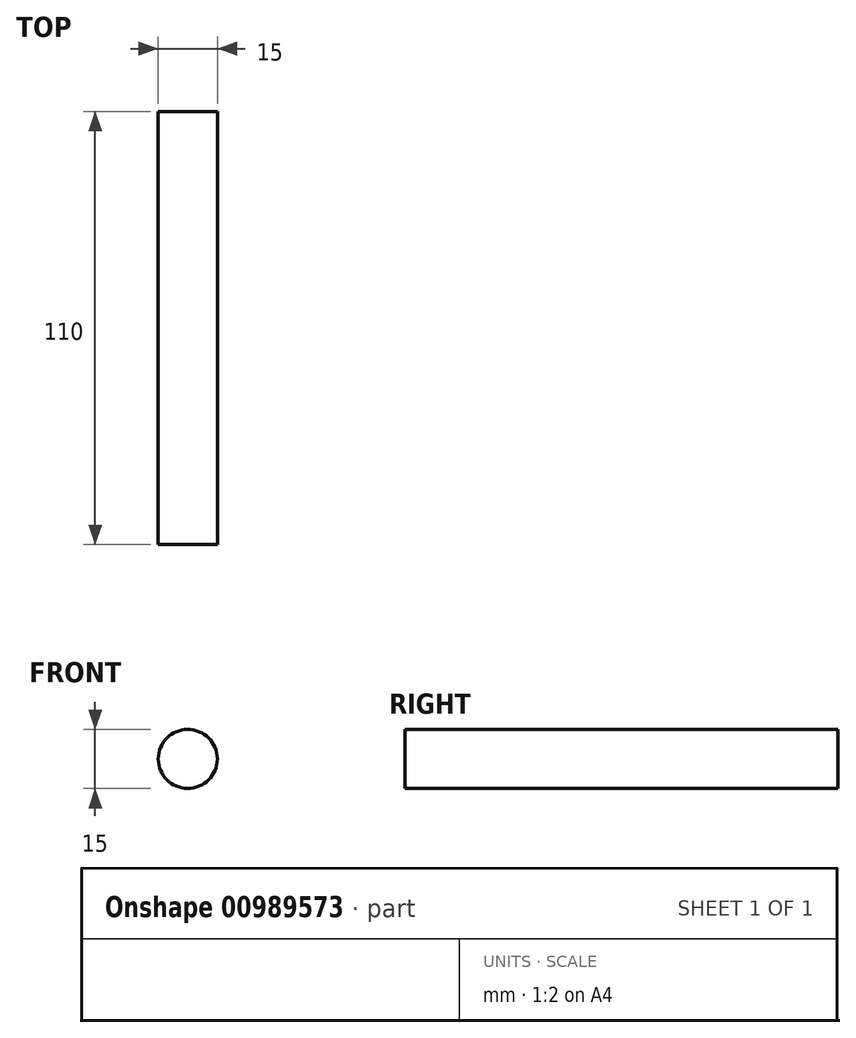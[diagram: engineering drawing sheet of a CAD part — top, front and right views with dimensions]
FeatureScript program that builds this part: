
annotation { "Feature Type Name" : "Feature", "Feature Type Description" : "" }
export const myFeature = defineFeature(function(context is Context, id is Id, definition is map)
    precondition{}
    {
        {
            var Q0;
            Q0=qCreatedBy(makeId("Front.planeOp"),FACE);
            var sketch = newSketch(context, id + "F0", { "sketchPlane" : qUnion([Q0])});
            skCircle(sketch, "E0", {"center": v(0, 0) * mm, "radius": 7.5 * mm});
            skSolve(sketch);
        }
        {
            var Q0;
            Q0 = qSketchRegion(id + "F0", true);
            extrude(context, id + "F1", {"entities" : qUnion([Q0]), "oppositeDirection" : true, "depth" : 110 * mm, "offsetDistance" : 25 * mm});
        }
    });
